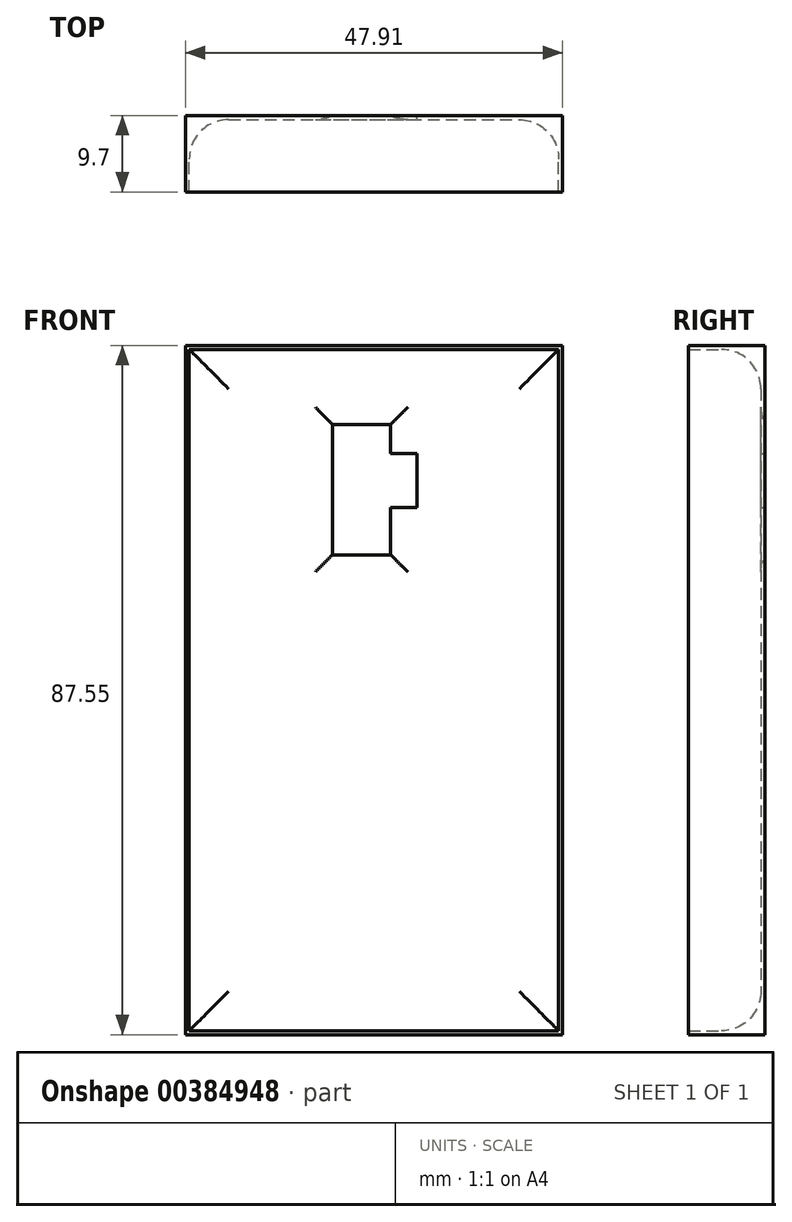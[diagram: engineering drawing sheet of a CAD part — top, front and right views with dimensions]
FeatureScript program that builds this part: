
annotation { "Feature Type Name" : "Feature", "Feature Type Description" : "" }
export const myFeature = defineFeature(function(context is Context, id is Id, definition is map)
    precondition{}
    {
        {
            var Q0;
            Q0=qCreatedBy(makeId("Front.planeOp"),FACE);
            var sketch = newSketch(context, id + "F0", { "sketchPlane" : qUnion([Q0])});
            skLineSegment(sketch, "E0.bottom", {"start": v(-23.66, 43.63) * mm, "end": v(24.25, 43.63) * mm});
            skLineSegment(sketch, "E0.top", {"start": v(-23.66, -43.92) * mm, "end": v(24.25, -43.92) * mm});
            skLineSegment(sketch, "E0.left", {"start": v(-23.66, 43.63) * mm, "end": v(-23.66, -43.92) * mm});
            skLineSegment(sketch, "E0.right", {"start": v(24.25, 43.63) * mm, "end": v(24.25, -43.92) * mm});
            skSolve(sketch);
        }
        {
            var Q0;
            Q0=makeQuery(id+"F0.imprint","IMPRINT",FACE,{"disambiguationData":[TD([[makeQuery(id+"F0.imprint","IMPRINT",EDGE,{"derivedFrom":sQuery(id+"F0.wireOp",EDGE,"E0.bottom")}),-1.0]])]});
            extrude(context, id + "F1", {"entities" : qUnion([Q0]), "depth" : 9.7 * mm});
        }
        {
            var Q0;
            Q0=makeQuery(id+"F1.opExtrude","CAP_FACE",FACE,{"disambiguationData":[OSD([sQuery(id+"F0.wireOp",EDGE,"E0.bottom"),sQuery(id+"F0.wireOp",EDGE,"E0.top"),sQuery(id+"F0.wireOp",EDGE,"E0.left"),sQuery(id+"F0.wireOp",EDGE,"E0.right")])],"isStart":false});
            shell(context, id + "F2", {"entities" : qUnion([Q0]), "thickness" : 0.5 * mm});
        }
        {
            var Q0;
            Q0=makeQuery(id+"F1.opExtrude","CAP_FACE",FACE,{"disambiguationData":[OSD([sQuery(id+"F0.wireOp",EDGE,"E0.bottom"),sQuery(id+"F0.wireOp",EDGE,"E0.top"),sQuery(id+"F0.wireOp",EDGE,"E0.left"),sQuery(id+"F0.wireOp",EDGE,"E0.right")])],"isStart":true});
            var sketch = newSketch(context, id + "F3", { "sketchPlane" : qUnion([Q0])});
            skLineSegment(sketch, "E1.bottom", {"start": v(-2.43, 33.61) * mm, "end": v(4.98, 33.61) * mm});
            skLineSegment(sketch, "E1.top", {"start": v(-2.43, 17.04) * mm, "end": v(4.98, 17.04) * mm});
            skLineSegment(sketch, "E1.left", {"start": v(-2.43, 33.61) * mm, "end": v(-2.43, 17.04) * mm});
            skLineSegment(sketch, "E1.right", {"start": v(4.98, 33.61) * mm, "end": v(4.98, 17.04) * mm});
            skSolve(sketch);
        }
        {
            var Q0;
            Q0=qSketchRegion(id+"F3",true);
            extrude(context, id + "F4", {"entities" : qUnion([Q0]), "operationType" : NewBodyOperationType.REMOVE, "oppositeDirection" : true, "depth" : 25 * mm});
        }
        {
            var Q0;
            Q0=makeQuery(id+"F1.opExtrude","CAP_FACE",FACE,{"disambiguationData":[OSD([sQuery(id+"F0.wireOp",EDGE,"E0.bottom"),sQuery(id+"F0.wireOp",EDGE,"E0.top"),sQuery(id+"F0.wireOp",EDGE,"E0.left"),sQuery(id+"F0.wireOp",EDGE,"E0.right")])],"isStart":true});
            var sketch = newSketch(context, id + "F5", { "sketchPlane" : qUnion([Q0])});
            skLineSegment(sketch, "E2.bottom", {"start": v(-5.76, 29.92) * mm, "end": v(-2.43, 29.92) * mm});
            skLineSegment(sketch, "E2.top", {"start": v(-5.76, 23.07) * mm, "end": v(-2.43, 23.07) * mm});
            skLineSegment(sketch, "E2.left", {"start": v(-5.76, 29.92) * mm, "end": v(-5.76, 23.07) * mm});
            skLineSegment(sketch, "E2.right", {"start": v(-2.43, 29.92) * mm, "end": v(-2.43, 23.07) * mm});
            skSolve(sketch);
        }
        {
            var Q0;
            Q0=makeQuery(id+"F2.opShell","OFFSET_FACE",FACE,{"disambiguationData":[OSD([sQuery(id+"F0.wireOp",EDGE,"E0.bottom"),sQuery(id+"F0.wireOp",EDGE,"E0.top"),sQuery(id+"F0.wireOp",EDGE,"E0.left"),sQuery(id+"F0.wireOp",EDGE,"E0.right")])]});
            fillet(context, id + "F6", {"entities" : qUnion([Q0]), "radius" : 5 * mm, "tangentPropagation" : true, "allowEdgeOverflow" : false});
        }
        {
            var Q0;
            Q0=qSketchRegion(id+"F5",true);
            extrude(context, id + "F7", {"entities" : qUnion([Q0]), "operationType" : NewBodyOperationType.REMOVE, "oppositeDirection" : true, "depth" : 25 * mm});
        }
    });
